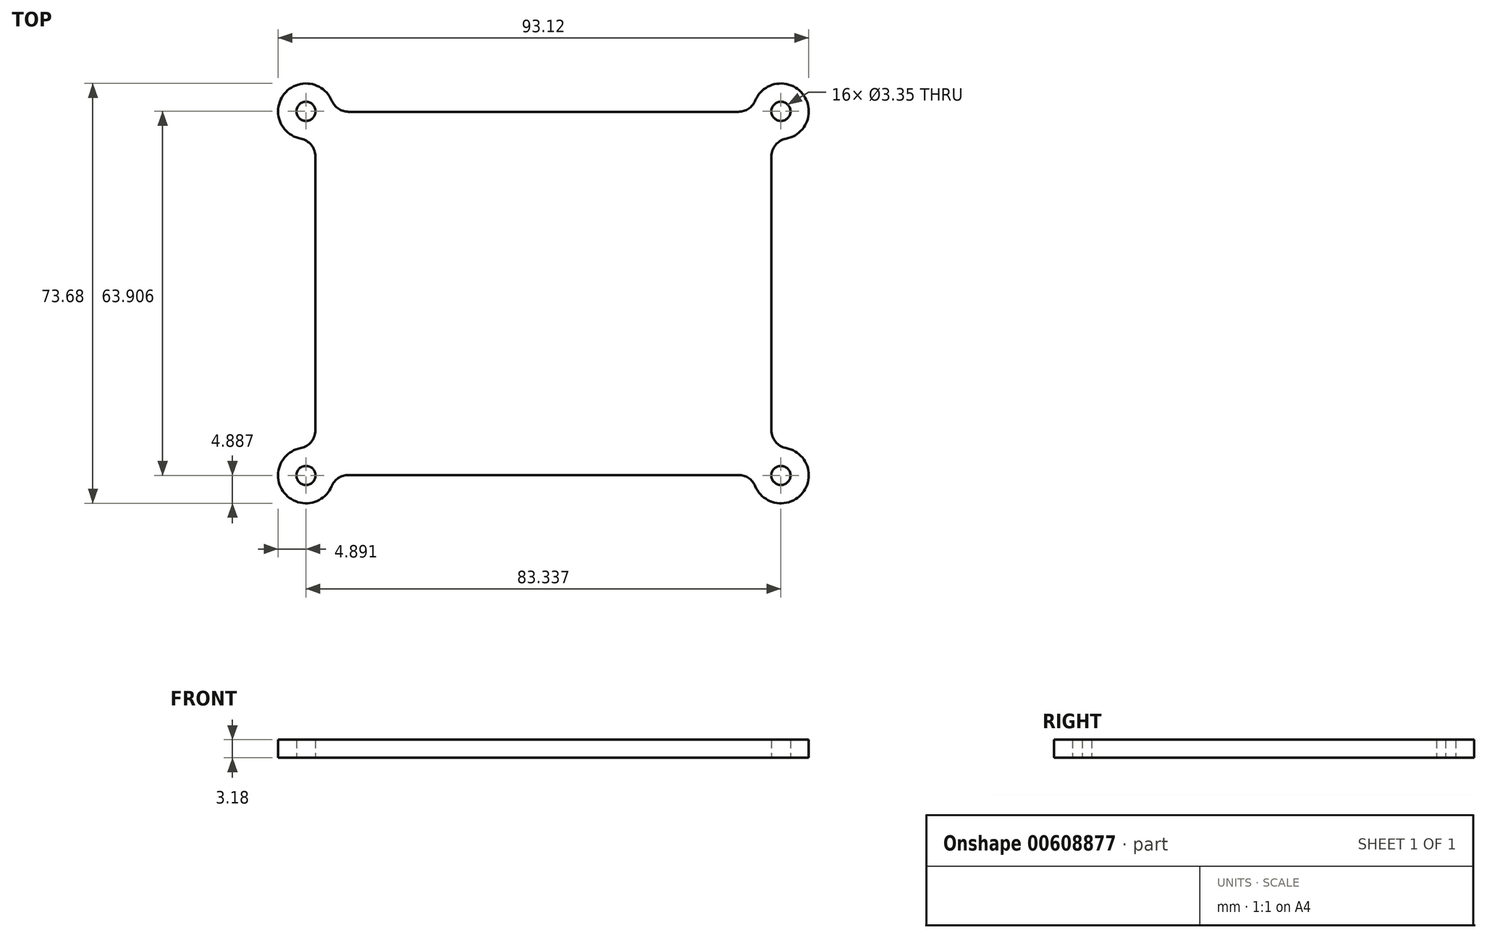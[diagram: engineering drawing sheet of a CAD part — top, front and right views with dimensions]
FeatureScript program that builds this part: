
annotation { "Feature Type Name" : "Feature", "Feature Type Description" : "" }
export const myFeature = defineFeature(function(context is Context, id is Id, definition is map)
    precondition{}
    {
        {
            var Q0;
            Q0=qCreatedBy(makeId("Top.planeOp"),FACE);
            var sketch = newSketch(context, id + "F0", { "sketchPlane" : qUnion([Q0])});
            skPoint(sketch, "E0.middle", {"position": v(0, 0) * mm});
            skLineSegment(sketch, "E1.bottom", {"start": v(-34.22, 31.88) * mm, "end": v(34.22, 31.88) * mm});
            skLineSegment(sketch, "E1.top", {"start": v(-34.22, -31.88) * mm, "end": v(34.22, -31.88) * mm});
            skLineSegment(sketch, "E1.left", {"start": v(-40, 24.03) * mm, "end": v(-40, 18.16) * mm});
            skLineSegment(sketch, "E1.right", {"start": v(40, 24.03) * mm, "end": v(40, -24.03) * mm});
            skArc(sketch, "E2", {"start": v(-37.15, 33.83) * mm, "mid": v(-45.46, 35.04) * mm, "end": v(-42.58, 27.15) * mm});
            skArc(sketch, "E3.filletArc", {"start": v(-37.15, 33.83) * mm, "mid": v(-35.98, 32.41) * mm, "end": v(-34.22, 31.88) * mm});
            skArc(sketch, "E4.filletArc", {"start": v(-40, 24.03) * mm, "mid": v(-40.73, 26.06) * mm, "end": v(-42.58, 27.15) * mm});
            skArc(sketch, "E5", {"start": v(-42.59, -27.15) * mm, "mid": v(-45.46, -35.04) * mm, "end": v(-37.15, -33.83) * mm});
            skArc(sketch, "E6.filletArc", {"start": v(-42.59, -27.15) * mm, "mid": v(-40.73, -26.06) * mm, "end": v(-40, -24.03) * mm});
            skArc(sketch, "E7.filletArc", {"start": v(-34.22, -31.88) * mm, "mid": v(-35.99, -32.41) * mm, "end": v(-37.15, -33.83) * mm});
            skArc(sketch, "E8", {"start": v(37.15, -33.83) * mm, "mid": v(45.46, -35.04) * mm, "end": v(42.59, -27.15) * mm});
            skArc(sketch, "E9.filletArc", {"start": v(40, -24.03) * mm, "mid": v(40.73, -26.06) * mm, "end": v(42.59, -27.15) * mm});
            skArc(sketch, "E10.filletArc", {"start": v(37.15, -33.83) * mm, "mid": v(35.99, -32.41) * mm, "end": v(34.22, -31.88) * mm});
            skArc(sketch, "E11", {"start": v(42.59, 27.15) * mm, "mid": v(45.46, 35.04) * mm, "end": v(37.15, 33.83) * mm});
            skArc(sketch, "E12.filletArc", {"start": v(34.22, 31.88) * mm, "mid": v(35.99, 32.41) * mm, "end": v(37.15, 33.83) * mm});
            skArc(sketch, "E13.filletArc", {"start": v(42.59, 27.15) * mm, "mid": v(40.73, 26.06) * mm, "end": v(40, 24.03) * mm});
            skCircle(sketch, "E14", {"center": v(-41.66, 31.95) * mm, "radius": 1.68 * mm});
            skCircle(sketch, "E15", {"center": v(-41.67, -31.95) * mm, "radius": 1.68 * mm});
            skCircle(sketch, "E16", {"center": v(41.67, -31.95) * mm, "radius": 1.68 * mm});
            skCircle(sketch, "E17", {"center": v(41.67, 31.95) * mm, "radius": 1.68 * mm});
            skLineSegment(sketch, "E18.trimOffspring", {"start": v(-40, 18.16) * mm, "end": v(-40, -23.75) * mm});
            skLineSegment(sketch, "E19.trimOffspring", {"start": v(-40, -23.75) * mm, "end": v(-40, -24.03) * mm});
            skSolve(sketch);
        }
        {
            var Q0;
            Q0=qSketchRegion(id+"F0",true);
            extrude(context, id + "F1", {"entities" : qUnion([Q0]), "depth" : 3.17 * mm, "offsetDistance" : 25.4 * mm});
        }
    });
